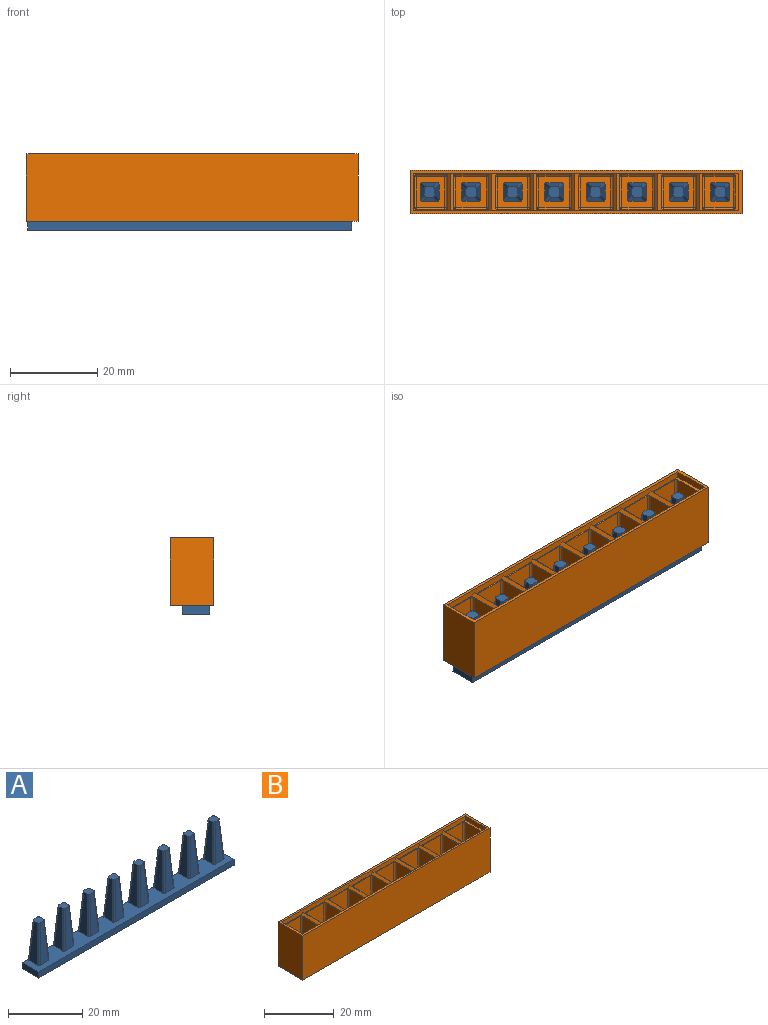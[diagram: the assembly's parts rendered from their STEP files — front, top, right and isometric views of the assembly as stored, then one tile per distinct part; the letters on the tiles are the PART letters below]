
ASSEMBLY  parts=2 mates=1
PART A: 78 faces, bbox 74.2x6.3x15 mm
  f0: plane 13x3.2mm, normal (-1,0,0.07), area 29.9mm2, adj f4,f5,f8,f9
  f1: plane 13x3.2mm, normal (0,-1,0.07), area 29.9mm2, adj f4,f5,f6,f9
  f2: plane 13x3.2mm, normal (1,0,0.07), area 29.9mm2, adj f4,f6,f7,f9
  f3: plane 13x3.2mm, normal (0,1,0.07), area 29.9mm2, adj f4,f7,f8,f74
  f4: plane 2.38x2.38mm, normal (0,0,1), area 5.5mm2, adj f0,f1,f2,f3,f5,f6,f7,f8
  f5: cylinder r=0.5mm len=13.03mm, axis (-0.07,-0.07,-1), area 10.2mm2, adj f0,f1,f4,f9
  f6: cylinder r=0.5mm len=13.03mm, axis (0.07,-0.07,-1), area 10.2mm2, adj f1,f2,f4,f9
  f7: cylinder r=0.5mm len=13.03mm, axis (0.07,0.07,-1), area 10.2mm2, adj f2,f3,f4,f9
  f8: cylinder r=0.5mm len=13.03mm, axis (-0.07,0.07,-1), area 10.2mm2, adj f0,f3,f4,f9
  f9: plane 74.2x6.2mm, normal (0,0,1), area 320.6mm2, adj f0,f1,f2,f5,f6,f7,f8,f11
  f10: plane 13x3.2mm, normal (0,1,0.07), area 29.9mm2, adj f14,f15,f18,f74
  f11: plane 13x3.2mm, normal (-1,0,0.07), area 29.9mm2, adj f9,f14,f15,f16
  f12: plane 13x3.2mm, normal (0,-1,0.07), area 29.9mm2, adj f9,f14,f16,f17
  f13: plane 13x3.2mm, normal (1,0,0.07), area 29.9mm2, adj f9,f14,f17,f18
  f14: plane 2.38x2.38mm, normal (0,0,1), area 5.5mm2, adj f10,f11,f12,f13,f15,f16,f17,f18
  f15: cylinder r=0.5mm len=13.03mm, axis (-0.07,0.07,-1), area 10.2mm2, adj f9,f10,f11,f14
  f16: cylinder r=0.5mm len=13.03mm, axis (-0.07,-0.07,-1), area 10.2mm2, adj f9,f11,f12,f14
  f17: cylinder r=0.5mm len=13.03mm, axis (0.07,-0.07,-1), area 10.2mm2, adj f9,f12,f13,f14
  f18: cylinder r=0.5mm len=13.03mm, axis (0.07,0.07,-1), area 10.2mm2, adj f9,f10,f13,f14
  f19: plane 13x3.2mm, normal (0,1,0.07), area 29.9mm2, adj f23,f24,f27,f74
  f20: plane 13x3.2mm, normal (-1,0,0.07), area 29.9mm2, adj f9,f23,f24,f25
  f21: plane 13x3.2mm, normal (0,-1,0.07), area 29.9mm2, adj f9,f23,f25,f26
  f22: plane 13x3.2mm, normal (1,0,0.07), area 29.9mm2, adj f9,f23,f26,f27
  f23: plane 2.38x2.38mm, normal (0,0,1), area 5.5mm2, adj f19,f20,f21,f22,f24,f25,f26,f27
  f24: cylinder r=0.5mm len=13.03mm, axis (-0.07,0.07,-1), area 10.2mm2, adj f9,f19,f20,f23
  f25: cylinder r=0.5mm len=13.03mm, axis (-0.07,-0.07,-1), area 10.2mm2, adj f9,f20,f21,f23
  f26: cylinder r=0.5mm len=13.03mm, axis (0.07,-0.07,-1), area 10.2mm2, adj f9,f21,f22,f23
  f27: cylinder r=0.5mm len=13.03mm, axis (0.07,0.07,-1), area 10.2mm2, adj f9,f19,f22,f23
  f28: plane 13x3.2mm, normal (0,1,0.07), area 29.9mm2, adj f32,f33,f36,f74
  f29: plane 13x3.2mm, normal (-1,0,0.07), area 29.9mm2, adj f9,f32,f33,f34
  f30: plane 13x3.2mm, normal (0,-1,0.07), area 29.9mm2, adj f9,f32,f34,f35
  f31: plane 13x3.2mm, normal (1,0,0.07), area 29.9mm2, adj f9,f32,f35,f36
  f32: plane 2.38x2.38mm, normal (0,0,1), area 5.5mm2, adj f28,f29,f30,f31,f33,f34,f35,f36
  f33: cylinder r=0.5mm len=13.03mm, axis (-0.07,0.07,-1), area 10.2mm2, adj f9,f28,f29,f32
  f34: cylinder r=0.5mm len=13.03mm, axis (-0.07,-0.07,-1), area 10.2mm2, adj f9,f29,f30,f32
  f35: cylinder r=0.5mm len=13.03mm, axis (0.07,-0.07,-1), area 10.2mm2, adj f9,f30,f31,f32
  f36: cylinder r=0.5mm len=13.03mm, axis (0.07,0.07,-1), area 10.2mm2, adj f9,f28,f31,f32
  f37: plane 13x3.2mm, normal (0,1,0.07), area 29.9mm2, adj f41,f42,f45,f74
  f38: plane 13x3.2mm, normal (-1,0,0.07), area 29.9mm2, adj f9,f41,f42,f43
  f39: plane 13x3.2mm, normal (0,-1,0.07), area 29.9mm2, adj f9,f41,f43,f44
  f40: plane 13x3.2mm, normal (1,0,0.07), area 29.9mm2, adj f9,f41,f44,f45
  f41: plane 2.38x2.38mm, normal (0,0,1), area 5.5mm2, adj f37,f38,f39,f40,f42,f43,f44,f45
  f42: cylinder r=0.5mm len=13.03mm, axis (-0.07,0.07,-1), area 10.2mm2, adj f9,f37,f38,f41
  f43: cylinder r=0.5mm len=13.03mm, axis (-0.07,-0.07,-1), area 10.2mm2, adj f9,f38,f39,f41
  f44: cylinder r=0.5mm len=13.03mm, axis (0.07,-0.07,-1), area 10.2mm2, adj f9,f39,f40,f41
  f45: cylinder r=0.5mm len=13.03mm, axis (0.07,0.07,-1), area 10.2mm2, adj f9,f37,f40,f41
  f46: plane 13x3.2mm, normal (0,1,0.07), area 29.9mm2, adj f50,f51,f54,f74
  f47: plane 13x3.2mm, normal (-1,0,0.07), area 29.9mm2, adj f9,f50,f51,f52
  f48: plane 13x3.2mm, normal (0,-1,0.07), area 29.9mm2, adj f9,f50,f52,f53
  f49: plane 13x3.2mm, normal (1,0,0.07), area 29.9mm2, adj f9,f50,f53,f54
  f50: plane 2.38x2.38mm, normal (0,0,1), area 5.5mm2, adj f46,f47,f48,f49,f51,f52,f53,f54
  f51: cylinder r=0.5mm len=13.03mm, axis (-0.07,0.07,-1), area 10.2mm2, adj f9,f46,f47,f50
  f52: cylinder r=0.5mm len=13.03mm, axis (-0.07,-0.07,-1), area 10.2mm2, adj f9,f47,f48,f50
  f53: cylinder r=0.5mm len=13.03mm, axis (0.07,-0.07,-1), area 10.2mm2, adj f9,f48,f49,f50
  f54: cylinder r=0.5mm len=13.03mm, axis (0.07,0.07,-1), area 10.2mm2, adj f9,f46,f49,f50
  f55: plane 13x3.2mm, normal (0,1,0.07), area 29.9mm2, adj f59,f60,f63,f74
  f56: plane 13x3.2mm, normal (-1,0,0.07), area 29.9mm2, adj f9,f59,f60,f61
  f57: plane 13x3.2mm, normal (0,-1,0.07), area 29.9mm2, adj f9,f59,f61,f62
  f58: plane 13x3.2mm, normal (1,0,0.07), area 29.9mm2, adj f9,f59,f62,f63
  f59: plane 2.38x2.38mm, normal (0,0,1), area 5.5mm2, adj f55,f56,f57,f58,f60,f61,f62,f63
  f60: cylinder r=0.5mm len=13.03mm, axis (-0.07,0.07,-1), area 10.2mm2, adj f9,f55,f56,f59
  f61: cylinder r=0.5mm len=13.03mm, axis (-0.07,-0.07,-1), area 10.2mm2, adj f9,f56,f57,f59
  f62: cylinder r=0.5mm len=13.03mm, axis (0.07,-0.07,-1), area 10.2mm2, adj f9,f57,f58,f59
  f63: cylinder r=0.5mm len=13.03mm, axis (0.07,0.07,-1), area 10.2mm2, adj f9,f55,f58,f59
  f64: plane 13x3.2mm, normal (0,1,0.07), area 29.9mm2, adj f68,f69,f72,f74
  f65: plane 13x3.2mm, normal (-1,0,0.07), area 29.9mm2, adj f9,f68,f69,f70
  f66: plane 13x3.2mm, normal (0,-1,0.07), area 29.9mm2, adj f9,f68,f70,f71
  f67: plane 13x3.2mm, normal (1,0,0.07), area 29.9mm2, adj f9,f68,f71,f72
  f68: plane 2.38x2.38mm, normal (0,0,1), area 5.5mm2, adj f64,f65,f66,f67,f69,f70,f71,f72
  f69: cylinder r=0.5mm len=13.03mm, axis (-0.07,0.07,-1), area 10.2mm2, adj f9,f64,f65,f68
  f70: cylinder r=0.5mm len=13.03mm, axis (-0.07,-0.07,-1), area 10.2mm2, adj f9,f65,f66,f68
  f71: cylinder r=0.5mm len=13.03mm, axis (0.07,-0.07,-1), area 10.2mm2, adj f9,f66,f67,f68
  f72: cylinder r=0.5mm len=13.03mm, axis (0.07,0.07,-1), area 10.2mm2, adj f9,f64,f67,f68
  f73: plane 6.34x2mm, normal (-1,0,0), area 12.5mm2, adj f9,f74,f76,f77
  f74: plane 74.2x2mm, normal (0,1,0.07), area 148.8mm2, adj f3,f9,f10,f19,f28,f37,f46,f55
  f75: plane 6.34x2mm, normal (1,0,0), area 12.5mm2, adj f9,f74,f76,f77
  f76: plane 74.2x2mm, normal (0,-1,0), area 148.4mm2, adj f9,f73,f75,f77
  f77: plane 74.2x6.34mm, normal (0,0,-1), area 470.4mm2, adj f73,f74,f75,f76
PART B: 255 faces, bbox 76x10x15.5 mm
  f0: plane 74.5x1.5mm, normal (0,1,0), area 108.2mm2, adj f1,f2,f3,f4,f5,f6,f7,f51
  f1: plane 8.5x8.09mm, normal (0,0,1), area 4.9mm2, adj f0,f21,f22,f23,f42,f213,f215,f218
  f2: plane 8.5x8.09mm, normal (0,0,1), area 4.9mm2, adj f0,f24,f25,f26,f43,f201,f203,f206
  f3: plane 8.5x8.09mm, normal (0,0,1), area 4.9mm2, adj f0,f27,f28,f29,f44,f189,f191,f194
  f4: plane 8.5x8.09mm, normal (0,0,1), area 4.9mm2, adj f0,f30,f31,f32,f45,f177,f179,f182
  f5: plane 8.5x8.09mm, normal (0,0,1), area 4.9mm2, adj f0,f33,f34,f35,f46,f165,f167,f170
  f6: plane 8.5x8.09mm, normal (0,0,1), area 4.9mm2, adj f0,f36,f37,f38,f47,f153,f155,f158
  f7: plane 8.5x7.79mm, normal (0,0,1), area 6.5mm2, adj f0,f8,f9,f49,f116,f141,f142,f147
  f8: plane 11.5x6.5mm, normal (0,1,0), area 74.8mm2, adj f7,f141,f146,f147
  f9: plane 11.5x6.5mm, normal (0,-1,0), area 74.8mm2, adj f7,f142,f148,f149
  f10: plane 7x6.5mm, normal (0,0,1), area 27mm2, adj f80,f81,f82,f83,f112,f113,f114,f115
  f11: plane 7x6.5mm, normal (0,0,1), area 27mm2, adj f52,f53,f54,f55,f84,f85,f86,f87
  f12: plane 7x7mm, normal (0,0,1), area 30.5mm2, adj f76,f77,f78,f79,f108,f109,f110,f111
  f13: plane 7x7mm, normal (0,0,1), area 30.5mm2, adj f72,f73,f74,f75,f104,f105,f106,f107
  f14: plane 7x7mm, normal (0,0,1), area 30.5mm2, adj f68,f69,f70,f71,f100,f101,f102,f103
  f15: plane 7x7mm, normal (0,0,1), area 30.5mm2, adj f64,f65,f66,f67,f96,f97,f98,f99
  f16: plane 7x7mm, normal (0,0,1), area 30.5mm2, adj f60,f61,f62,f63,f92,f93,f94,f95
  f17: plane 7x7mm, normal (0,0,1), area 30.5mm2, adj f56,f57,f58,f59,f88,f89,f90,f91
  f18: plane 76x10mm, normal (0,0,-1), area 592.4mm2, adj f39,f40,f41,f48,f52,f53,f54,f55
  f19: plane 11.5x7mm, normal (1,0,0), area 80.5mm2, adj f51,f129,f130,f131
  f20: plane 11.5x6.5mm, normal (0,-1,0), area 74.7mm2, adj f51,f131,f136,f137
  f21: plane 11.5x7mm, normal (1,0,0), area 80.5mm2, adj f1,f218,f222,f224
  f22: plane 11.5x7mm, normal (0,-1,0), area 80.5mm2, adj f1,f215,f221,f224
  f23: plane 11.5x7mm, normal (-1,0,0), area 80.5mm2, adj f1,f213,f215,f216
  f24: plane 11.5x7mm, normal (1,0,0), area 80.5mm2, adj f2,f206,f210,f212
  f25: plane 11.5x7mm, normal (0,-1,0), area 80.5mm2, adj f2,f203,f209,f212
  f26: plane 11.5x7mm, normal (-1,0,0), area 80.5mm2, adj f2,f201,f203,f204
  f27: plane 11.5x7mm, normal (1,0,0), area 80.5mm2, adj f3,f194,f198,f200
  f28: plane 11.5x7mm, normal (0,-1,0), area 80.5mm2, adj f3,f191,f197,f200
  f29: plane 11.5x7mm, normal (-1,0,0), area 80.5mm2, adj f3,f189,f191,f192
  f30: plane 11.5x7mm, normal (1,0,0), area 80.5mm2, adj f4,f182,f186,f188
  f31: plane 11.5x7mm, normal (0,-1,0), area 80.5mm2, adj f4,f179,f185,f188
  f32: plane 11.5x7mm, normal (-1,0,0), area 80.5mm2, adj f4,f177,f179,f180
  f33: plane 11.5x7mm, normal (1,0,0), area 80.5mm2, adj f5,f170,f174,f176
  f34: plane 11.5x7mm, normal (0,-1,0), area 80.5mm2, adj f5,f167,f173,f176
  f35: plane 11.5x7mm, normal (-1,0,0), area 80.5mm2, adj f5,f165,f167,f168
  f36: plane 11.5x7mm, normal (1,0,0), area 80.5mm2, adj f6,f158,f162,f164
  f37: plane 11.5x7mm, normal (0,-1,0), area 80.5mm2, adj f6,f155,f161,f164
  f38: plane 11.5x7mm, normal (-1,0,0), area 80.5mm2, adj f6,f153,f155,f156
  f39: plane 76x15.5mm, normal (0,-1,0), area 1178mm2, adj f18,f40,f48,f228
  f40: plane 15.5x10mm, normal (1,0,0), area 155mm2, adj f18,f39,f41,f228
  f41: plane 76x15.5mm, normal (0,1,0), area 1178mm2, adj f18,f40,f48,f228
  f42: plane 11.5x7mm, normal (0,1,0), area 80.5mm2, adj f1,f213,f217,f218
  f43: plane 11.5x7mm, normal (0,1,0), area 80.5mm2, adj f2,f201,f205,f206
  f44: plane 11.5x7mm, normal (0,1,0), area 80.5mm2, adj f3,f189,f193,f194
  f45: plane 11.5x7mm, normal (0,1,0), area 80.5mm2, adj f4,f177,f181,f182
  f46: plane 11.5x7mm, normal (0,1,0), area 80.5mm2, adj f5,f165,f169,f170
  f47: plane 11.5x7mm, normal (0,1,0), area 80.5mm2, adj f6,f153,f157,f158
  f48: plane 15.5x10mm, normal (-1,0,0), area 155mm2, adj f18,f39,f41,f228
  f49: plane 11.5x7mm, normal (-1,0,0), area 80.5mm2, adj f7,f141,f142,f143
  f50: plane 11.5x6.5mm, normal (0,1,0), area 74.7mm2, adj f51,f129,f134,f135
  f51: plane 8.5x8.29mm, normal (0,0,1), area 10.7mm2, adj f0,f19,f20,f50,f117,f129,f131,f134
  f52: plane 3.6x2mm, normal (0,1,-0.07), area 6.9mm2, adj f11,f18,f84,f87
  f53: plane 3.6x2mm, normal (1,0,-0.07), area 6.9mm2, adj f11,f18,f86,f87
  f54: plane 3.6x2mm, normal (0,-1,-0.07), area 6.9mm2, adj f11,f18,f85,f86
  f55: plane 3.6x2mm, normal (-1,0,-0.07), area 6.9mm2, adj f11,f18,f84,f85
  f56: plane 3.6x2mm, normal (0,1,-0.07), area 6.9mm2, adj f17,f18,f88,f91
  f57: plane 3.6x2mm, normal (1,0,-0.07), area 6.9mm2, adj f17,f18,f90,f91
  f58: plane 3.6x2mm, normal (0,-1,-0.07), area 6.9mm2, adj f17,f18,f89,f90
  f59: plane 3.6x2mm, normal (-1,0,-0.07), area 6.9mm2, adj f17,f18,f88,f89
  f60: plane 3.6x2mm, normal (0,1,-0.07), area 6.9mm2, adj f16,f18,f92,f95
  f61: plane 3.6x2mm, normal (1,0,-0.07), area 6.9mm2, adj f16,f18,f94,f95
  f62: plane 3.6x2mm, normal (0,-1,-0.07), area 6.9mm2, adj f16,f18,f93,f94
  f63: plane 3.6x2mm, normal (-1,0,-0.07), area 6.9mm2, adj f16,f18,f92,f93
  f64: plane 3.6x2mm, normal (0,1,-0.07), area 6.9mm2, adj f15,f18,f96,f99
  f65: plane 3.6x2mm, normal (1,0,-0.07), area 6.9mm2, adj f15,f18,f98,f99
  f66: plane 3.6x2mm, normal (0,-1,-0.07), area 6.9mm2, adj f15,f18,f97,f98
  f67: plane 3.6x2mm, normal (-1,0,-0.07), area 6.9mm2, adj f15,f18,f96,f97
  f68: plane 3.6x2mm, normal (0,1,-0.07), area 6.9mm2, adj f14,f18,f100,f103
  f69: plane 3.6x2mm, normal (1,0,-0.07), area 6.9mm2, adj f14,f18,f102,f103
  f70: plane 3.6x2mm, normal (0,-1,-0.07), area 6.9mm2, adj f14,f18,f101,f102
  f71: plane 3.6x2mm, normal (-1,0,-0.07), area 6.9mm2, adj f14,f18,f100,f101
  f72: plane 3.6x2mm, normal (0,1,-0.07), area 6.9mm2, adj f13,f18,f104,f107
  f73: plane 3.6x2mm, normal (1,0,-0.07), area 6.9mm2, adj f13,f18,f106,f107
  f74: plane 3.6x2mm, normal (0,-1,-0.07), area 6.9mm2, adj f13,f18,f105,f106
  f75: plane 3.6x2mm, normal (-1,0,-0.07), area 6.9mm2, adj f13,f18,f104,f105
  f76: plane 3.6x2mm, normal (0,1,-0.07), area 6.9mm2, adj f12,f18,f108,f111
  f77: plane 3.6x2mm, normal (1,0,-0.07), area 6.9mm2, adj f12,f18,f108,f109
  f78: plane 3.6x2mm, normal (0,-1,-0.07), area 6.9mm2, adj f12,f18,f109,f110
  f79: plane 3.6x2mm, normal (-1,0,-0.07), area 6.9mm2, adj f12,f18,f110,f111
  f80: plane 3.6x2mm, normal (1,0,-0.07), area 6.9mm2, adj f10,f18,f112,f115
  f81: plane 3.6x2mm, normal (0,-1,-0.07), area 6.9mm2, adj f10,f18,f114,f115
  f82: plane 3.6x2mm, normal (-1,0,-0.07), area 6.9mm2, adj f10,f18,f113,f114
  f83: plane 3.6x2mm, normal (0,1,-0.07), area 6.9mm2, adj f10,f18,f112,f113
  f84: cylinder r=0.5mm len=2.03mm, axis (-0.07,0.07,1), area 1.6mm2, adj f11,f18,f52,f55
  f85: cylinder r=0.5mm len=2.03mm, axis (-0.07,-0.07,1), area 1.6mm2, adj f11,f18,f54,f55
  f86: cylinder r=0.5mm len=2.03mm, axis (0.07,-0.07,1), area 1.6mm2, adj f11,f18,f53,f54
  f87: cylinder r=0.5mm len=2.03mm, axis (0.07,0.07,1), area 1.6mm2, adj f11,f18,f52,f53
  f88: cylinder r=0.5mm len=2.03mm, axis (-0.07,0.07,1), area 1.6mm2, adj f17,f18,f56,f59
  f89: cylinder r=0.5mm len=2.03mm, axis (-0.07,-0.07,1), area 1.6mm2, adj f17,f18,f58,f59
  f90: cylinder r=0.5mm len=2.03mm, axis (0.07,-0.07,1), area 1.6mm2, adj f17,f18,f57,f58
  f91: cylinder r=0.5mm len=2.03mm, axis (0.07,0.07,1), area 1.6mm2, adj f17,f18,f56,f57
  f92: cylinder r=0.5mm len=2.03mm, axis (-0.07,0.07,1), area 1.6mm2, adj f16,f18,f60,f63
  f93: cylinder r=0.5mm len=2.03mm, axis (-0.07,-0.07,1), area 1.6mm2, adj f16,f18,f62,f63
  f94: cylinder r=0.5mm len=2.03mm, axis (0.07,-0.07,1), area 1.6mm2, adj f16,f18,f61,f62
  f95: cylinder r=0.5mm len=2.03mm, axis (0.07,0.07,1), area 1.6mm2, adj f16,f18,f60,f61
  f96: cylinder r=0.5mm len=2.03mm, axis (-0.07,0.07,1), area 1.6mm2, adj f15,f18,f64,f67
  f97: cylinder r=0.5mm len=2.03mm, axis (-0.07,-0.07,1), area 1.6mm2, adj f15,f18,f66,f67
  f98: cylinder r=0.5mm len=2.03mm, axis (0.07,-0.07,1), area 1.6mm2, adj f15,f18,f65,f66
  f99: cylinder r=0.5mm len=2.03mm, axis (0.07,0.07,1), area 1.6mm2, adj f15,f18,f64,f65
  f100: cylinder r=0.5mm len=2.03mm, axis (-0.07,0.07,1), area 1.6mm2, adj f14,f18,f68,f71
  f101: cylinder r=0.5mm len=2.03mm, axis (-0.07,-0.07,1), area 1.6mm2, adj f14,f18,f70,f71
  f102: cylinder r=0.5mm len=2.03mm, axis (0.07,-0.07,1), area 1.6mm2, adj f14,f18,f69,f70
  f103: cylinder r=0.5mm len=2.03mm, axis (0.07,0.07,1), area 1.6mm2, adj f14,f18,f68,f69
  f104: cylinder r=0.5mm len=2.03mm, axis (-0.07,0.07,1), area 1.6mm2, adj f13,f18,f72,f75
  f105: cylinder r=0.5mm len=2.03mm, axis (-0.07,-0.07,1), area 1.6mm2, adj f13,f18,f74,f75
  f106: cylinder r=0.5mm len=2.03mm, axis (0.07,-0.07,1), area 1.6mm2, adj f13,f18,f73,f74
  f107: cylinder r=0.5mm len=2.03mm, axis (0.07,0.07,1), area 1.6mm2, adj f13,f18,f72,f73
  f108: cylinder r=0.5mm len=2.03mm, axis (0.07,0.07,1), area 1.6mm2, adj f12,f18,f76,f77
  f109: cylinder r=0.5mm len=2.03mm, axis (0.07,-0.07,1), area 1.6mm2, adj f12,f18,f77,f78
  f110: cylinder r=0.5mm len=2.03mm, axis (-0.07,-0.07,1), area 1.6mm2, adj f12,f18,f78,f79
  f111: cylinder r=0.5mm len=2.03mm, axis (-0.07,0.07,1), area 1.6mm2, adj f12,f18,f76,f79
  f112: cylinder r=0.5mm len=2.03mm, axis (0.07,0.07,1), area 1.6mm2, adj f10,f18,f80,f83
  f113: cylinder r=0.5mm len=2.03mm, axis (-0.07,0.07,1), area 1.6mm2, adj f10,f18,f82,f83
  f114: cylinder r=0.5mm len=2.03mm, axis (-0.07,-0.07,1), area 1.6mm2, adj f10,f18,f81,f82
  f115: cylinder r=0.5mm len=2.03mm, axis (0.07,-0.07,1), area 1.6mm2, adj f10,f18,f80,f81
  f116: plane 11.5x7mm, normal (1,0,0), area 73.7mm2, adj f7,f118,f119,f120,f121,f122,f123,f124
  f117: plane 11.5x7mm, normal (-1,0,0), area 80.5mm2, adj f51,f134,f137,f140
  f118: plane 2.46x0.6mm, normal (0,1,0), area 1.5mm2, adj f116,f119,f127,f128
  f119: plane 2.39x0.6mm, normal (0,0,1), area 1.4mm2, adj f116,f118,f120,f128
  f120: plane 0.6x0.6mm, normal (0,1,0), area 0.4mm2, adj f116,f119,f121,f128
  f121: plane 2.39x0.6mm, normal (0,0,-1), area 1.4mm2, adj f116,f120,f122,f128
  f122: plane 2.11x0.6mm, normal (0,1,0), area 1.3mm2, adj f116,f121,f123,f128
  f123: plane 2.54x0.6mm, normal (0,0,1), area 1.5mm2, adj f116,f122,f124,f128
  f124: plane 0.6x0.6mm, normal (0,1,0), area 0.4mm2, adj f116,f123,f125,f128
  f125: plane 3.21x0.6mm, normal (0,0,-1), area 1.9mm2, adj f116,f124,f126,f128
  f126: plane 5.76x0.6mm, normal (0,-1,0), area 3.5mm2, adj f116,f125,f127,f128
  f127: plane 0.67x0.6mm, normal (0,0,1), area 0.4mm2, adj f116,f118,f126,f128
  f128: plane 5.76x3.21mm, normal (1,0,0), area 6.8mm2, adj f118,f119,f120,f121,f122,f123,f124,f125
  f129: cylinder r=0.5mm len=11.5mm, axis (0,0,1), area 9mm2, adj f19,f50,f51,f132
  f130: cylinder r=0.5mm len=7mm, axis (0,-1,0), area 5.5mm2, adj f11,f19,f132,f133
  f131: cylinder r=0.5mm len=11.5mm, axis (0,0,-1), area 9mm2, adj f19,f20,f51,f133
  f132: sphere r=0.5mm, area 0.4mm2, adj f129,f130,f135
  f133: sphere r=0.5mm, area 0.4mm2, adj f130,f131,f136
  f134: cylinder r=0.5mm len=11.5mm, axis (0,0,-1), area 9mm2, adj f50,f51,f117,f138
  f135: cylinder r=0.5mm len=6.5mm, axis (1,0,0), area 5.1mm2, adj f11,f50,f132,f138
  f136: cylinder r=0.5mm len=6.5mm, axis (-1,0,0), area 5.1mm2, adj f11,f20,f133,f139
  f137: cylinder r=0.5mm len=11.5mm, axis (0,0,1), area 9mm2, adj f20,f51,f117,f139
  f138: sphere r=0.5mm, area 0.4mm2, adj f134,f135,f140
  f139: sphere r=0.5mm, area 0.4mm2, adj f136,f137,f140
  f140: cylinder r=0.5mm len=7mm, axis (0,1,0), area 5.5mm2, adj f11,f117,f138,f139
  f141: cylinder r=0.5mm len=11.5mm, axis (0,0,-1), area 9mm2, adj f7,f8,f49,f144
  f142: cylinder r=0.5mm len=11.5mm, axis (0,0,1), area 9mm2, adj f7,f9,f49,f145
  f143: cylinder r=0.5mm len=7mm, axis (0,1,0), area 5.5mm2, adj f10,f49,f144,f145
  f144: sphere r=0.5mm, area 0.4mm2, adj f141,f143,f146
  f145: sphere r=0.5mm, area 0.4mm2, adj f142,f143,f149
  f146: cylinder r=0.5mm len=6.5mm, axis (1,0,0), area 5.1mm2, adj f8,f10,f144,f150
  f147: cylinder r=0.5mm len=11.5mm, axis (0,0,1), area 9mm2, adj f7,f8,f116,f150
  f148: cylinder r=0.5mm len=11.5mm, axis (0,0,-1), area 9mm2, adj f7,f9,f116,f151
  f149: cylinder r=0.5mm len=6.5mm, axis (-1,0,0), area 5.1mm2, adj f9,f10,f145,f151
  f150: sphere r=0.5mm, area 0.4mm2, adj f146,f147,f152
  f151: sphere r=0.5mm, area 0.4mm2, adj f148,f149,f152
  f152: cylinder r=0.5mm len=7mm, axis (0,-1,0), area 5.5mm2, adj f10,f116,f150,f151
  f153: cylinder r=0.5mm len=11.5mm, axis (0,0,-1), area 9mm2, adj f6,f38,f47,f154
  f154: sphere r=0.5mm, area 0.4mm2, adj f153,f156,f157
  f155: cylinder r=0.5mm len=11.5mm, axis (0,0,1), area 9mm2, adj f6,f37,f38,f159
  f156: cylinder r=0.5mm len=7mm, axis (0,1,0), area 5.5mm2, adj f12,f38,f154,f159
  f157: cylinder r=0.5mm len=7mm, axis (1,0,0), area 5.5mm2, adj f12,f47,f154,f160
  f158: cylinder r=0.5mm len=11.5mm, axis (0,0,1), area 9mm2, adj f6,f36,f47,f160
  f159: sphere r=0.5mm, area 0.4mm2, adj f155,f156,f161
  f160: sphere r=0.5mm, area 0.4mm2, adj f157,f158,f162
  f161: cylinder r=0.5mm len=7mm, axis (-1,0,0), area 5.5mm2, adj f12,f37,f159,f163
  f162: cylinder r=0.5mm len=7mm, axis (0,-1,0), area 5.5mm2, adj f12,f36,f160,f163
  f163: sphere r=0.5mm, area 0.4mm2, adj f161,f162,f164
  f164: cylinder r=0.5mm len=11.5mm, axis (0,0,-1), area 9mm2, adj f6,f36,f37,f163
  f165: cylinder r=0.5mm len=11.5mm, axis (0,0,-1), area 9mm2, adj f5,f35,f46,f166
  f166: sphere r=0.5mm, area 0.4mm2, adj f165,f168,f169
  f167: cylinder r=0.5mm len=11.5mm, axis (0,0,1), area 9mm2, adj f5,f34,f35,f171
  f168: cylinder r=0.5mm len=7mm, axis (0,1,0), area 5.5mm2, adj f13,f35,f166,f171
  f169: cylinder r=0.5mm len=7mm, axis (1,0,0), area 5.5mm2, adj f13,f46,f166,f172
  f170: cylinder r=0.5mm len=11.5mm, axis (0,0,1), area 9mm2, adj f5,f33,f46,f172
  f171: sphere r=0.5mm, area 0.4mm2, adj f167,f168,f173
  f172: sphere r=0.5mm, area 0.4mm2, adj f169,f170,f174
  f173: cylinder r=0.5mm len=7mm, axis (-1,0,0), area 5.5mm2, adj f13,f34,f171,f175
  f174: cylinder r=0.5mm len=7mm, axis (0,-1,0), area 5.5mm2, adj f13,f33,f172,f175
  f175: sphere r=0.5mm, area 0.4mm2, adj f173,f174,f176
  f176: cylinder r=0.5mm len=11.5mm, axis (0,0,-1), area 9mm2, adj f5,f33,f34,f175
  f177: cylinder r=0.5mm len=11.5mm, axis (0,0,-1), area 9mm2, adj f4,f32,f45,f178
  f178: sphere r=0.5mm, area 0.4mm2, adj f177,f180,f181
  f179: cylinder r=0.5mm len=11.5mm, axis (0,0,1), area 9mm2, adj f4,f31,f32,f183
  f180: cylinder r=0.5mm len=7mm, axis (0,1,0), area 5.5mm2, adj f14,f32,f178,f183
  f181: cylinder r=0.5mm len=7mm, axis (1,0,0), area 5.5mm2, adj f14,f45,f178,f184
  f182: cylinder r=0.5mm len=11.5mm, axis (0,0,1), area 9mm2, adj f4,f30,f45,f184
  f183: sphere r=0.5mm, area 0.4mm2, adj f179,f180,f185
  f184: sphere r=0.5mm, area 0.4mm2, adj f181,f182,f186
  f185: cylinder r=0.5mm len=7mm, axis (-1,0,0), area 5.5mm2, adj f14,f31,f183,f187
  f186: cylinder r=0.5mm len=7mm, axis (0,-1,0), area 5.5mm2, adj f14,f30,f184,f187
  f187: sphere r=0.5mm, area 0.4mm2, adj f185,f186,f188
  f188: cylinder r=0.5mm len=11.5mm, axis (0,0,-1), area 9mm2, adj f4,f30,f31,f187
  f189: cylinder r=0.5mm len=11.5mm, axis (0,0,-1), area 9mm2, adj f3,f29,f44,f190
  f190: sphere r=0.5mm, area 0.4mm2, adj f189,f192,f193
  f191: cylinder r=0.5mm len=11.5mm, axis (0,0,1), area 9mm2, adj f3,f28,f29,f195
  f192: cylinder r=0.5mm len=7mm, axis (0,1,0), area 5.5mm2, adj f15,f29,f190,f195
  f193: cylinder r=0.5mm len=7mm, axis (1,0,0), area 5.5mm2, adj f15,f44,f190,f196
  f194: cylinder r=0.5mm len=11.5mm, axis (0,0,1), area 9mm2, adj f3,f27,f44,f196
  f195: sphere r=0.5mm, area 0.4mm2, adj f191,f192,f197
  f196: sphere r=0.5mm, area 0.4mm2, adj f193,f194,f198
  f197: cylinder r=0.5mm len=7mm, axis (-1,0,0), area 5.5mm2, adj f15,f28,f195,f199
  f198: cylinder r=0.5mm len=7mm, axis (0,-1,0), area 5.5mm2, adj f15,f27,f196,f199
  f199: sphere r=0.5mm, area 0.4mm2, adj f197,f198,f200
  f200: cylinder r=0.5mm len=11.5mm, axis (0,0,-1), area 9mm2, adj f3,f27,f28,f199
  f201: cylinder r=0.5mm len=11.5mm, axis (0,0,-1), area 9mm2, adj f2,f26,f43,f202
  f202: sphere r=0.5mm, area 0.4mm2, adj f201,f204,f205
  f203: cylinder r=0.5mm len=11.5mm, axis (0,0,1), area 9mm2, adj f2,f25,f26,f207
  f204: cylinder r=0.5mm len=7mm, axis (0,1,0), area 5.5mm2, adj f16,f26,f202,f207
  f205: cylinder r=0.5mm len=7mm, axis (1,0,0), area 5.5mm2, adj f16,f43,f202,f208
  f206: cylinder r=0.5mm len=11.5mm, axis (0,0,1), area 9mm2, adj f2,f24,f43,f208
  f207: sphere r=0.5mm, area 0.4mm2, adj f203,f204,f209
  f208: sphere r=0.5mm, area 0.4mm2, adj f205,f206,f210
  f209: cylinder r=0.5mm len=7mm, axis (-1,0,0), area 5.5mm2, adj f16,f25,f207,f211
  f210: cylinder r=0.5mm len=7mm, axis (0,-1,0), area 5.5mm2, adj f16,f24,f208,f211
  f211: sphere r=0.5mm, area 0.4mm2, adj f209,f210,f212
  f212: cylinder r=0.5mm len=11.5mm, axis (0,0,-1), area 9mm2, adj f2,f24,f25,f211
  f213: cylinder r=0.5mm len=11.5mm, axis (0,0,-1), area 9mm2, adj f1,f23,f42,f214
  f214: sphere r=0.5mm, area 0.4mm2, adj f213,f216,f217
  f215: cylinder r=0.5mm len=11.5mm, axis (0,0,1), area 9mm2, adj f1,f22,f23,f219
  f216: cylinder r=0.5mm len=7mm, axis (0,1,0), area 5.5mm2, adj f17,f23,f214,f219
  f217: cylinder r=0.5mm len=7mm, axis (1,0,0), area 5.5mm2, adj f17,f42,f214,f220
  f218: cylinder r=0.5mm len=11.5mm, axis (0,0,1), area 9mm2, adj f1,f21,f42,f220
  f219: sphere r=0.5mm, area 0.4mm2, adj f215,f216,f221
  f220: sphere r=0.5mm, area 0.4mm2, adj f217,f218,f222
  f221: cylinder r=0.5mm len=7mm, axis (-1,0,0), area 5.5mm2, adj f17,f22,f219,f223
  f222: cylinder r=0.5mm len=7mm, axis (0,-1,0), area 5.5mm2, adj f17,f21,f220,f223
  f223: sphere r=0.5mm, area 0.4mm2, adj f221,f222,f224
  f224: cylinder r=0.5mm len=11.5mm, axis (0,0,-1), area 9mm2, adj f1,f21,f22,f223
  f225: plane 8.5x1.5mm, normal (1,0,0), area 12.7mm2, adj f0,f7,f226,f228
  f226: plane 74.5x1.5mm, normal (0,-1,0), area 108.2mm2, adj f1,f2,f3,f4,f5,f6,f7,f51
  f227: plane 8.5x1.5mm, normal (-1,0,0), area 12.7mm2, adj f0,f51,f226,f228
  f228: plane 76x10mm, normal (0,0,1), area 126.8mm2, adj f0,f39,f40,f41,f48,f225,f226,f227
  f229: plane 8.5x0.71mm, normal (0.71,0,0.71), area 8.5mm2, adj f0,f6,f226,f230
  f230: plane 8.5x0.71mm, normal (-0.71,0,0.71), area 8.5mm2, adj f0,f7,f226,f229
  f231: plane 8.5x0.71mm, normal (-0.71,0,0.71), area 8.5mm2, adj f0,f6,f226,f232
  f232: plane 8.5x0.71mm, normal (0.71,0,0.71), area 8.5mm2, adj f0,f5,f226,f231
  f233: plane 8.5x0.71mm, normal (-0.71,0,0.71), area 8.5mm2, adj f0,f5,f226,f234
  f234: plane 8.5x0.71mm, normal (0.71,0,0.71), area 8.5mm2, adj f0,f4,f226,f233
  f235: plane 8.5x0.71mm, normal (-0.71,0,0.71), area 8.5mm2, adj f0,f4,f226,f236
  f236: plane 8.5x0.71mm, normal (0.71,0,0.71), area 8.5mm2, adj f0,f3,f226,f235
  f237: plane 8.5x0.71mm, normal (-0.71,0,0.71), area 8.5mm2, adj f0,f3,f226,f238
  f238: plane 8.5x0.71mm, normal (0.71,0,0.71), area 8.5mm2, adj f0,f2,f226,f237
  f239: plane 8.5x0.71mm, normal (-0.71,0,0.71), area 8.5mm2, adj f0,f2,f226,f240
  f240: plane 8.5x0.71mm, normal (0.71,0,0.71), area 8.5mm2, adj f0,f1,f226,f239
  f241: plane 8.5x0.71mm, normal (-0.71,0,0.71), area 8.5mm2, adj f0,f1,f226,f242
  f242: plane 8.5x0.71mm, normal (0.71,0,0.71), area 8.5mm2, adj f0,f51,f226,f241
  f243: plane 2.51x0.6mm, normal (0,-1,0), area 1.5mm2, adj f244,f252,f253,f254
  f244: plane 2.43x0.6mm, normal (0,0,1), area 1.5mm2, adj f243,f245,f253,f254
  f245: plane 0.61x0.6mm, normal (0,-1,0), area 0.4mm2, adj f244,f246,f253,f254
  f246: plane 2.43x0.6mm, normal (0,0,-1), area 1.5mm2, adj f245,f247,f253,f254
  f247: plane 2.15x0.6mm, normal (0,-1,0), area 1.3mm2, adj f246,f248,f253,f254
  f248: plane 2.59x0.6mm, normal (0,0,1), area 1.6mm2, adj f247,f249,f253,f254
  f249: plane 0.61x0.6mm, normal (0,-1,0), area 0.4mm2, adj f248,f250,f253,f254
  f250: plane 3.27x0.6mm, normal (0,0,-1), area 2mm2, adj f249,f251,f253,f254
  f251: plane 5.87x0.6mm, normal (0,1,0), area 3.5mm2, adj f250,f252,f253,f254
  f252: plane 0.68x0.6mm, normal (0,0,1), area 0.4mm2, adj f243,f251,f253,f254
  f253: plane 5.87x3.27mm, normal (-1,0,0), area 7.1mm2, adj f243,f244,f245,f246,f247,f248,f249,f250
  f254: plane 5.87x3.27mm, normal (1,0,0), area 7.1mm2, adj f243,f244,f245,f246,f247,f248,f249,f250
PLACE A t=(7.27,13.53,-9.44)mm
PLACE B t=(2.76,18.53,-7.44)mm
MATE planar B.f18 <-> A.f9  axis (0,0,-1) through (14.46,11.73,-9.44)mm
